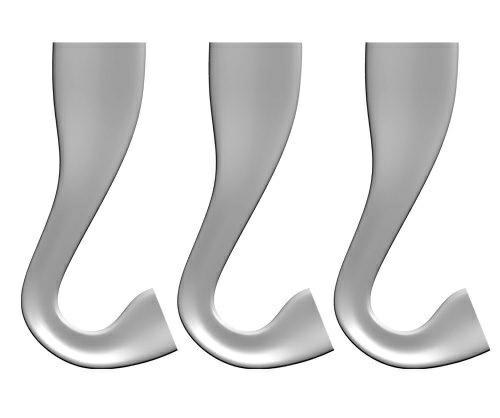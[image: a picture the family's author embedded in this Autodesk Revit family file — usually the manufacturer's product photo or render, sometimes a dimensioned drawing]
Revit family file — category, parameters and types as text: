
# Revit family: CITY ALPHABET letter „W”
name_source: partatom
category: Furniture
revit_build: Autodesk Revit 2018 (Build: 20190510_1515(x64)
units: mm (PartAtom-declared; Revit-internal decimal feet)

## family parameters
Cut with Voids When Loaded = No
Host = Face
OmniClass Number = 23.40.10.11.14
OmniClass Title = Exterior Seating
Room Calculation Point = No
Shared = No

## types (1)
- CITY ALPHABET letter „W”
    Default Elevation = 1219 mm
    Height = 420 mm  [stored 1.37795 ft]
    IfcExportAs = IfcFurnishingElement
    Length = 3350 mm  [stored 10.9908 ft]
    Manufacturer = Astrini Design
    Material information = Colour choice from RAL colour standard. Customer may inquire about specific request regarding individual order.
    Model = CITY ALPHABET letter „W”
    Operating temperature = -40°C to 80°C, ( -40°F to 176°F )
    Type Comments = Bench
    Type Image = W.jpg
    URL = https://astrini-design.pl
    Weight (approximately) = 104.00 kg
    Weight - filled (approximately) = 254.00 kg
    Width = 2350 mm

note: [stored X ft] marks values corroborated as IEEE doubles in the binary element streams (Revit-internal decimal feet)
